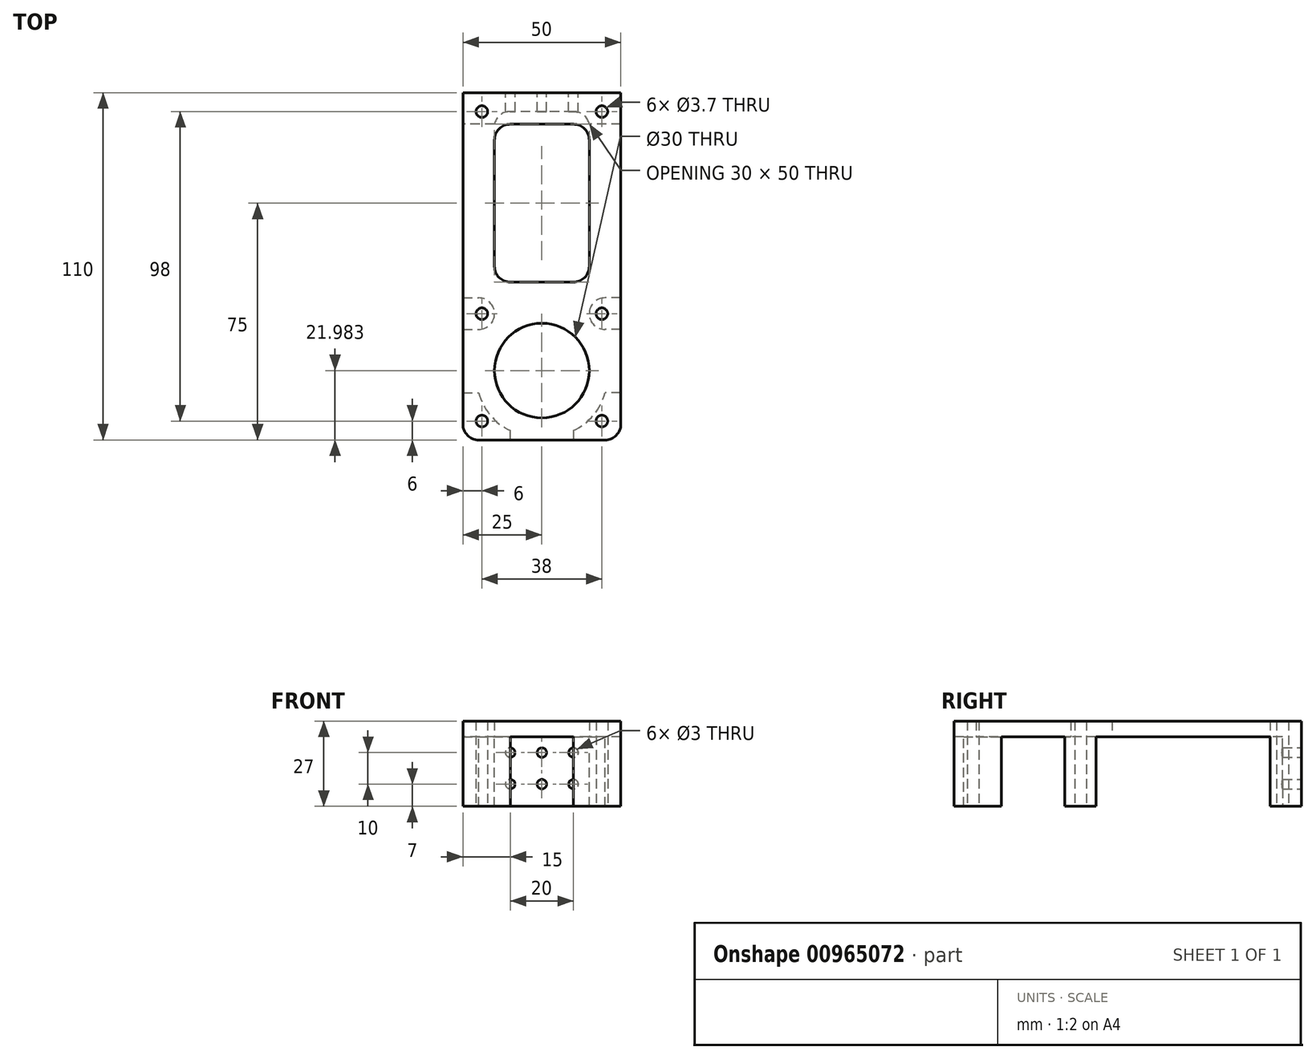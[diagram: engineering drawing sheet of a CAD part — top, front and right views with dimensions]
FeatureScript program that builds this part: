
annotation { "Feature Type Name" : "Feature", "Feature Type Description" : "" }
export const myFeature = defineFeature(function(context is Context, id is Id, definition is map)
    precondition{}
    {
        {
            var Q0;
            Q0=qCreatedBy(makeId("Top.planeOp"),FACE);
            var sketch = newSketch(context, id + "F0", { "sketchPlane" : qUnion([Q0])});
            skLineSegment(sketch, "E0.bottom", {"start": v(0, 0) * mm, "end": v(50, 0) * mm});
            skLineSegment(sketch, "E0.top", {"start": v(0, 110) * mm, "end": v(50, 110) * mm});
            skLineSegment(sketch, "E0.left", {"start": v(0, 0) * mm, "end": v(0, 110) * mm});
            skLineSegment(sketch, "E0.right", {"start": v(50, 0) * mm, "end": v(50, 110) * mm});
            skCircle(sketch, "E1", {"center": v(6, 6) * mm, "radius": 1.85 * mm});
            skCircle(sketch, "E2", {"center": v(44, 6) * mm, "radius": 1.85 * mm});
            skLineSegment(sketch, "E3", {"start": v(50, 15) * mm, "end": v(45, 15) * mm});
            skArc(sketch, "E4", {"start": v(35, 3) * mm, "mid": v(41.34, 7.88) * mm, "end": v(45, 15) * mm});
            skLineSegment(sketch, "E5", {"start": v(35, 3) * mm, "end": v(35, 0) * mm});
            skLineSegment(sketch, "E6", {"start": v(0, 15) * mm, "end": v(5, 15) * mm});
            skLineSegment(sketch, "E7", {"start": v(15, 0) * mm, "end": v(15, 3) * mm});
            skArc(sketch, "E8", {"start": v(5, 15) * mm, "mid": v(8.66, 7.88) * mm, "end": v(15, 3) * mm});
            skCircle(sketch, "E9", {"center": v(44, 40) * mm, "radius": 1.85 * mm});
            skCircle(sketch, "E10", {"center": v(6, 40) * mm, "radius": 1.85 * mm});
            skCircle(sketch, "E11", {"center": v(25, 21.98) * mm, "radius": 15 * mm});
            skLineSegment(sketch, "E12.bottom", {"start": v(50, 45) * mm, "end": v(40, 45) * mm});
            skLineSegment(sketch, "E12.top", {"start": v(50, 35) * mm, "end": v(40, 35) * mm});
            skLineSegment(sketch, "E12.left", {"start": v(50, 45) * mm, "end": v(50, 35) * mm});
            skLineSegment(sketch, "E12.right", {"start": v(40, 45) * mm, "end": v(40, 35) * mm});
            skLineSegment(sketch, "E13.bottom", {"start": v(0, 45) * mm, "end": v(10, 45) * mm});
            skLineSegment(sketch, "E13.top", {"start": v(0, 35) * mm, "end": v(10, 35) * mm});
            skLineSegment(sketch, "E13.left", {"start": v(0, 45) * mm, "end": v(0, 35) * mm});
            skLineSegment(sketch, "E13.right", {"start": v(10, 45) * mm, "end": v(10, 35) * mm});
            skLineSegment(sketch, "E14.bottom", {"start": v(35, 100) * mm, "end": v(15, 100) * mm});
            skLineSegment(sketch, "E14.top", {"start": v(35, 50) * mm, "end": v(15, 50) * mm});
            skLineSegment(sketch, "E14.left", {"start": v(40, 95) * mm, "end": v(40, 55) * mm});
            skLineSegment(sketch, "E14.right", {"start": v(10, 95) * mm, "end": v(10, 55) * mm});
            skPoint(sketch, "E15.visualSharp", {"position": v(10, 100) * mm});
            skArc(sketch, "E15.filletArc", {"start": v(15, 100) * mm, "mid": v(11.46, 98.54) * mm, "end": v(10, 95) * mm});
            skPoint(sketch, "E16.visualSharp", {"position": v(40, 100) * mm});
            skArc(sketch, "E16.filletArc", {"start": v(40, 95) * mm, "mid": v(38.54, 98.54) * mm, "end": v(35, 100) * mm});
            skPoint(sketch, "E17.visualSharp", {"position": v(40, 50) * mm});
            skArc(sketch, "E17.filletArc", {"start": v(35, 50) * mm, "mid": v(38.54, 51.46) * mm, "end": v(40, 55) * mm});
            skPoint(sketch, "E18.visualSharp", {"position": v(10, 50) * mm});
            skArc(sketch, "E18.filletArc", {"start": v(10, 55) * mm, "mid": v(11.46, 51.46) * mm, "end": v(15, 50) * mm});
            skCircle(sketch, "E19", {"center": v(6, 104) * mm, "radius": 1.85 * mm});
            skCircle(sketch, "E20", {"center": v(44, 104) * mm, "radius": 1.85 * mm});
            skLineSegment(sketch, "E21", {"start": v(50, 100) * mm, "end": v(40, 100) * mm});
            skLineSegment(sketch, "E22", {"start": v(40, 100) * mm, "end": v(40, 104) * mm});
            skLineSegment(sketch, "E23", {"start": v(40, 104) * mm, "end": v(10, 104) * mm});
            skLineSegment(sketch, "E24", {"start": v(10, 104) * mm, "end": v(10, 100) * mm});
            skLineSegment(sketch, "E25", {"start": v(10, 100) * mm, "end": v(0, 100) * mm});
            skSolve(sketch);
        }
        {
            var Q0;
            Q0=makeQuery(id+"F0.imprint","IMPRINT",FACE,{"disambiguationData":[TD([[makeQuery(id+"F0.imprint","IMPRINT",EDGE,{"derivedFrom":sQuery(id+"F0.wireOp",EDGE,"E0.bottom")}),1.0]])]});
            var Q1;
            {var subQ1=sQuery(id+"F0.wireOp",EDGE,"E0.top");Q1=makeQuery(id+"F0.imprint","IMPRINT",FACE,{"disambiguationData":[TD([[makeQuery(id+"F0.imprint","IMPRINT",EDGE,{"derivedFrom":subQ1}),-1.0]])]});}
            var Q2;
            Q2=makeQuery(id+"F0.imprint","IMPRINT",FACE,{"disambiguationData":[TD([[makeQuery(id+"F0.imprint","IMPRINT",EDGE,{"derivedFrom":sQuery(id+"F0.wireOp",EDGE,"E10")}),-1.0]])]});
            var Q3;
            Q3=makeQuery(id+"F0.imprint","IMPRINT",FACE,{"disambiguationData":[TD([[makeQuery(id+"F0.imprint","IMPRINT",EDGE,{"derivedFrom":sQuery(id+"F0.wireOp",EDGE,"E9")}),-1.0]])]});
            var Q4;
            {var subQ7=sQuery(id+"F0.wireOp",EDGE,"E3");Q4=makeQuery(id+"F0.imprint","IMPRINT",FACE,{"disambiguationData":[TD([[makeQuery(id+"F0.imprint","IMPRINT",EDGE,{"derivedFrom":subQ7}),-1.0]])]});}
            extrude(context, id + "F1", {"entities" : qUnion([Q0, Q1, Q2, Q3, Q4]), "depth" : 5 * mm, "offsetDistance" : 25 * mm});
        }
        {
            var Q0;
            Q0=makeQuery(id+"F0.imprint","IMPRINT",FACE,{"disambiguationData":[TD([[makeQuery(id+"F0.imprint","IMPRINT",EDGE,{"derivedFrom":sQuery(id+"F0.wireOp",EDGE,"E2")}),-1.0]])]});
            var Q1;
            Q1=makeQuery(id+"F0.imprint","IMPRINT",FACE,{"disambiguationData":[TD([[makeQuery(id+"F0.imprint","IMPRINT",EDGE,{"derivedFrom":sQuery(id+"F0.wireOp",EDGE,"E1")}),-1.0]])]});
            var Q2;
            Q2=makeQuery(id+"F0.imprint","IMPRINT",FACE,{"disambiguationData":[TD([[makeQuery(id+"F0.imprint","IMPRINT",EDGE,{"derivedFrom":sQuery(id+"F0.wireOp",EDGE,"E9")}),-1.0]])]});
            var Q3;
            Q3=makeQuery(id+"F0.imprint","IMPRINT",FACE,{"disambiguationData":[TD([[makeQuery(id+"F0.imprint","IMPRINT",EDGE,{"derivedFrom":sQuery(id+"F0.wireOp",EDGE,"E10")}),-1.0]])]});
            var Q4;
            Q4=makeQuery(id+"F0.imprint","IMPRINT",FACE,{"disambiguationData":[TD([[makeQuery(id+"F0.imprint","IMPRINT",EDGE,{"derivedFrom":sQuery(id+"F0.wireOp",EDGE,"E20")}),-1.0]])]});
            var Q5;
            Q5=makeQuery(id+"F0.imprint","IMPRINT",FACE,{"disambiguationData":[TD([[makeQuery(id+"F0.imprint","IMPRINT",EDGE,{"derivedFrom":sQuery(id+"F0.wireOp",EDGE,"E19")}),-1.0]])]});
            extrude(context, id + "F2", {"entities" : qUnion([Q0, Q1, Q2, Q3, Q4, Q5]), "operationType" : NewBodyOperationType.ADD, "oppositeDirection" : true, "depth" : 22 * mm, "offsetDistance" : 25 * mm});
        }
        {
            var Q0;
            {var subQ0=sQuery(id+"F0.wireOp",EDGE,"E0.right");var subQ1=sQuery(id+"F0.wireOp",EDGE,"E0.bottom");Q0=makeQuery(id+"F2.boolean.opBoolean","MERGE",EDGE,{"derivedFrom":[makeQuery(id+"F1.opExtrude","SWEPT_EDGE",EDGE,{"disambiguationData":[OSD([subQ1,subQ0])]}),makeQuery(id+"F2.opExtrude","SWEPT_EDGE",EDGE,{"disambiguationData":[OSD([subQ1,subQ0])]})]});}
            var Q1;
            {var subQ0=sQuery(id+"F0.wireOp",EDGE,"E0.left");var subQ1=sQuery(id+"F0.wireOp",EDGE,"E0.bottom");Q1=makeQuery(id+"F2.boolean.opBoolean","MERGE",EDGE,{"derivedFrom":[makeQuery(id+"F1.opExtrude","SWEPT_EDGE",EDGE,{"disambiguationData":[OSD([subQ1,subQ0])]}),makeQuery(id+"F2.opExtrude","SWEPT_EDGE",EDGE,{"disambiguationData":[OSD([subQ1,subQ0])]})]});}
            var Q2;
            Q2=makeQuery(id+"F2.opExtrude","SWEPT_EDGE",EDGE,{"disambiguationData":[OSD([sQuery(id+"F0.wireOp",EDGE,"E12.top"),sQuery(id+"F0.wireOp",EDGE,"E12.right")])]});
            var Q3;
            Q3=makeQuery(id+"F2.opExtrude","SWEPT_EDGE",EDGE,{"disambiguationData":[OSD([sQuery(id+"F0.wireOp",EDGE,"E12.bottom"),sQuery(id+"F0.wireOp",EDGE,"E12.right")])]});
            var Q4;
            Q4=makeQuery(id+"F2.opExtrude","SWEPT_EDGE",EDGE,{"disambiguationData":[OSD([sQuery(id+"F0.wireOp",EDGE,"E13.top"),sQuery(id+"F0.wireOp",EDGE,"E13.right")])]});
            var Q5;
            Q5=makeQuery(id+"F2.opExtrude","SWEPT_EDGE",EDGE,{"disambiguationData":[OSD([sQuery(id+"F0.wireOp",EDGE,"E13.bottom"),sQuery(id+"F0.wireOp",EDGE,"E13.right")])]});
            var Q6;
            Q6=makeQuery(id+"F2.opExtrude","SWEPT_EDGE",EDGE,{"disambiguationData":[OSD([sQuery(id+"F0.wireOp",EDGE,"kOq96LRQ-1Vjb-ucUl-8lEl-9DbM6hDz8irG.top"),sQuery(id+"F0.wireOp",EDGE,"kOq96LRQ-1Vjb-ucUl-8lEl-9DbM6hDz8irG.right")])]});
            var Q7;
            Q7=makeQuery(id+"F2.opExtrude","SWEPT_EDGE",EDGE,{"disambiguationData":[OSD([sQuery(id+"F0.wireOp",EDGE,"Xux2o5Cu-0eVk-gegj-TURz-DC8JWWQIGhTF.top"),sQuery(id+"F0.wireOp",EDGE,"Xux2o5Cu-0eVk-gegj-TURz-DC8JWWQIGhTF.right")])]});
            fillet(context, id + "F3", {"entities" : qUnion([Q0, Q1, Q2, Q3, Q4, Q5, Q6, Q7]), "tangentPropagation" : true, "radius" : 5 * mm, "defaultsChanged" : false, "vertexSettings" : [], "allowEdgeOverflow" : false});
        }
        {
            var Q0;
            Q0=makeQuery(id+"F2.opExtrude","SWEPT_EDGE",EDGE,{"disambiguationData":[OSD([sQuery(id+"F0.wireOp",EDGE,"E22"),sQuery(id+"F0.wireOp",EDGE,"E23")])]});
            var Q1;
            Q1=makeQuery(id+"F2.opExtrude","SWEPT_EDGE",EDGE,{"disambiguationData":[OSD([sQuery(id+"F0.wireOp",EDGE,"E23"),sQuery(id+"F0.wireOp",EDGE,"E24")])]});
            fillet(context, id + "F4", {"entities" : qUnion([Q0, Q1]), "tangentPropagation" : true, "radius" : 5 * mm, "defaultsChanged" : false, "vertexSettings" : [], "allowEdgeOverflow" : false});
        }
        {
            var Q0;
            {var subQ0=sQuery(id+"F0.wireOp",EDGE,"E0.top");Q0=makeQuery(id+"F2.boolean.opBoolean","MERGE",FACE,{"derivedFrom":[makeQuery(id+"F1.opExtrude","SWEPT_FACE",FACE,{"disambiguationData":[OSD([subQ0])]}),makeQuery(id+"F2.opExtrude","SWEPT_FACE",FACE,{"disambiguationData":[OSD([subQ0])]})]});}
            var sketch = newSketch(context, id + "F5", { "sketchPlane" : qUnion([Q0])});
            skCircle(sketch, "E26", {"center": v(-35, -5) * mm, "radius": 1.5 * mm});
            skCircle(sketch, "E27", {"center": v(-15, -5) * mm, "radius": 1.5 * mm});
            skCircle(sketch, "E28", {"center": v(-35, -15) * mm, "radius": 1.5 * mm});
            skCircle(sketch, "E29", {"center": v(-15, -15) * mm, "radius": 1.5 * mm});
            skCircle(sketch, "E30", {"center": v(-25, -5) * mm, "radius": 1.5 * mm});
            skCircle(sketch, "E31", {"center": v(-25, -15) * mm, "radius": 1.5 * mm});
            skSolve(sketch);
        }
        {
            var Q0;
            Q0=makeQuery(id+"F5.imprint","IMPRINT",FACE,{"disambiguationData":[TD([[makeQuery(id+"F5.imprint","IMPRINT",EDGE,{"derivedFrom":sQuery(id+"F5.wireOp",EDGE,"E28")}),1.0]])]});
            var Q1;
            Q1=makeQuery(id+"F5.imprint","IMPRINT",FACE,{"disambiguationData":[TD([[makeQuery(id+"F5.imprint","IMPRINT",EDGE,{"derivedFrom":sQuery(id+"F5.wireOp",EDGE,"E26")}),1.0]])]});
            var Q2;
            Q2=makeQuery(id+"F5.imprint","IMPRINT",FACE,{"disambiguationData":[TD([[makeQuery(id+"F5.imprint","IMPRINT",EDGE,{"derivedFrom":sQuery(id+"F5.wireOp",EDGE,"E27")}),1.0]])]});
            var Q3;
            Q3=makeQuery(id+"F5.imprint","IMPRINT",FACE,{"disambiguationData":[TD([[makeQuery(id+"F5.imprint","IMPRINT",EDGE,{"derivedFrom":sQuery(id+"F5.wireOp",EDGE,"E29")}),1.0]])]});
            var Q4;
            Q4=makeQuery(id+"F5.imprint","IMPRINT",FACE,{"disambiguationData":[TD([[makeQuery(id+"F5.imprint","IMPRINT",EDGE,{"derivedFrom":sQuery(id+"F5.wireOp",EDGE,"E31")}),1.0]])]});
            var Q5;
            Q5=makeQuery(id+"F5.imprint","IMPRINT",FACE,{"disambiguationData":[TD([[makeQuery(id+"F5.imprint","IMPRINT",EDGE,{"derivedFrom":sQuery(id+"F5.wireOp",EDGE,"E30")}),1.0]])]});
            extrude(context, id + "F6", {"entities" : qUnion([Q0, Q1, Q2, Q3, Q4, Q5]), "operationType" : NewBodyOperationType.REMOVE, "oppositeDirection" : true, "depth" : 25 * mm, "offsetDistance" : 25 * mm});
        }
    });
